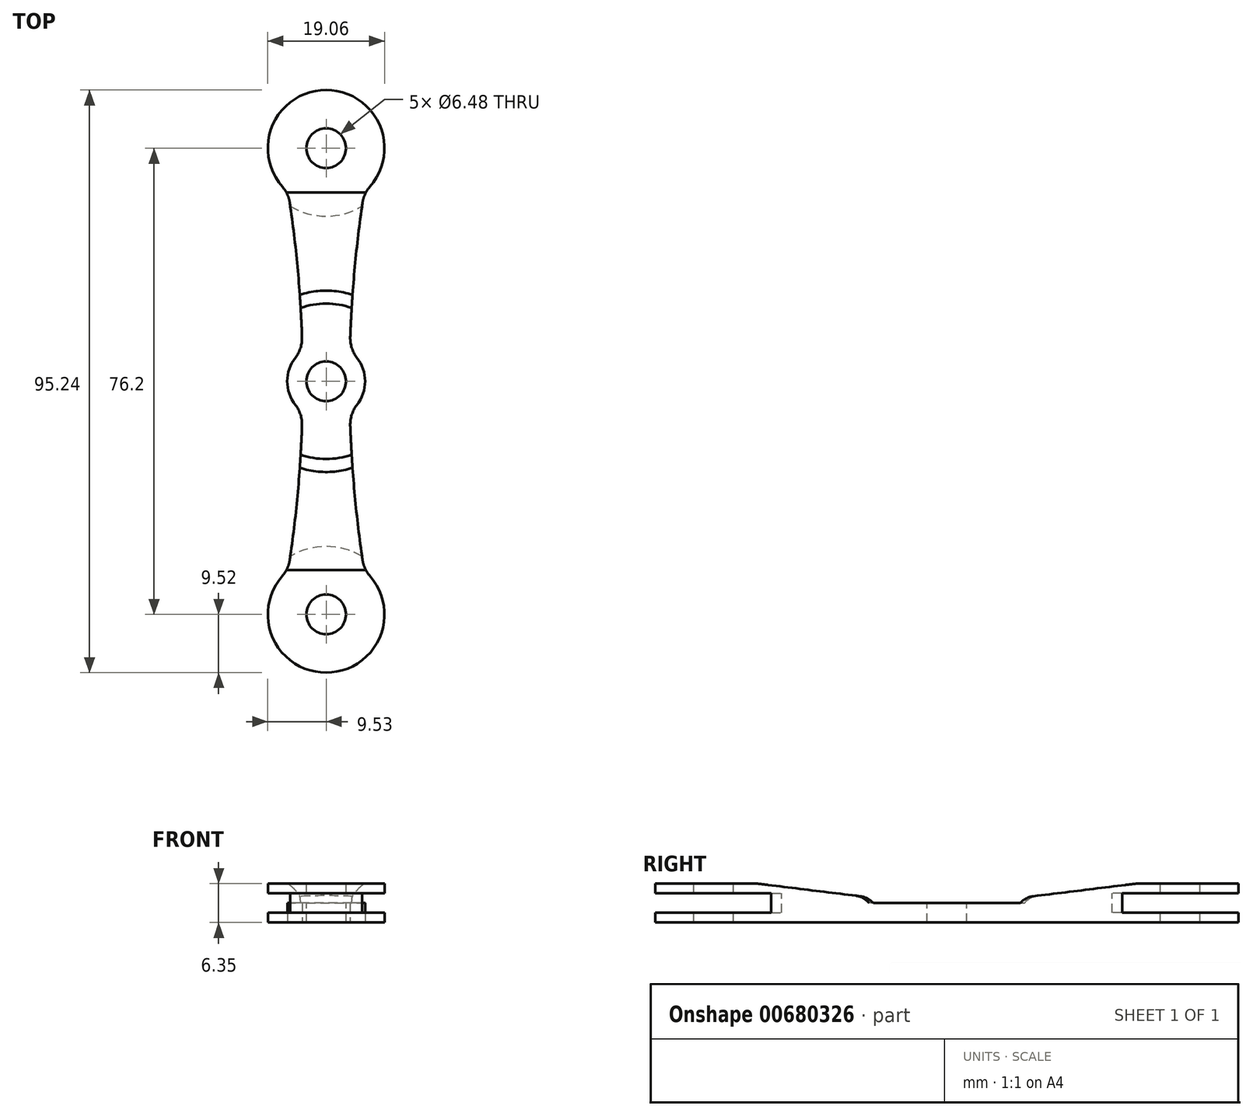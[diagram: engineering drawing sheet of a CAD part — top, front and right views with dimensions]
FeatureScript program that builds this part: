
annotation { "Feature Type Name" : "Feature", "Feature Type Description" : "" }
export const myFeature = defineFeature(function(context is Context, id is Id, definition is map)
    precondition{}
    {
        {
            var Q0;
            Q0=qCreatedBy(makeId("Top.planeOp"),FACE);
            var sketch = newSketch(context, id + "F0", { "sketchPlane" : qUnion([Q0])});
            skLineSegment(sketch, "E0.bottom", {"start": v(9.52, 47.63) * mm, "end": v(-9.53, 47.63) * mm});
            skLineSegment(sketch, "E0.top", {"start": v(9.52, -47.63) * mm, "end": v(-9.53, -47.63) * mm});
            skLineSegment(sketch, "E0.left", {"start": v(9.52, 47.63) * mm, "end": v(9.52, -47.63) * mm});
            skLineSegment(sketch, "E0.right", {"start": v(-9.52, 47.63) * mm, "end": v(-9.53, -47.63) * mm});
            skPoint(sketch, "E0.middle", {"position": v(0, 0) * mm});
            skCircle(sketch, "E1", {"center": v(0, 38.1) * mm, "radius": 9.53 * mm});
            skCircle(sketch, "E2", {"center": v(0, -38.1) * mm, "radius": 9.52 * mm});
            skCircle(sketch, "E3", {"center": v(0, 0) * mm, "radius": 6.35 * mm});
            skArc(sketch, "E4", {"start": v(-9.53, -47.62) * mm, "mid": v(-3.81, 0) * mm, "end": v(-9.53, 47.63) * mm});
            skArc(sketch, "E5", {"start": v(9.53, 47.62) * mm, "mid": v(3.81, 0) * mm, "end": v(9.53, -47.62) * mm});
            skSolve(sketch);
        }
        {
            var Q0;
            {var subQ0=sQuery(id+"F0.wireOp",EDGE,"E4");var subQ1=sQuery(id+"F0.wireOp",EDGE,"E3");var subQ2=makeQuery(id+"F0.imprint","INTERSECT",VERTEX,{"disambiguationData":[OD(0.0)],"derivedFrom":[subQ1,subQ0]});Q0=makeQuery(id+"F0.imprint","IMPRINT",FACE,{"disambiguationData":[TD([[makeQuery(id+"F0.imprint","IMPRINT",EDGE,{"disambiguationData":[TD([[subQ2,1.0]])],"derivedFrom":subQ1}),1.0]])]});}
            var Q1;
            {var subQ0=sQuery(id+"F0.wireOp",EDGE,"E5");var subQ1=sQuery(id+"F0.wireOp",EDGE,"E3");var subQ2=makeQuery(id+"F0.imprint","INTERSECT",VERTEX,{"disambiguationData":[OD(0.0)],"derivedFrom":[subQ1,subQ0]});Q1=makeQuery(id+"F0.imprint","IMPRINT",FACE,{"disambiguationData":[TD([[makeQuery(id+"F0.imprint","IMPRINT",EDGE,{"disambiguationData":[TD([[subQ2,1.0]])],"derivedFrom":subQ1}),1.0]])]});}
            var Q2;
            {var subQ0=sQuery(id+"F0.wireOp",EDGE,"E4");var subQ1=sQuery(id+"F0.wireOp",EDGE,"E3");var subQ2=makeQuery(id+"F0.imprint","INTERSECT",VERTEX,{"disambiguationData":[OD(0.0)],"derivedFrom":[subQ1,subQ0]});Q2=makeQuery(id+"F0.imprint","IMPRINT",FACE,{"disambiguationData":[TD([[makeQuery(id+"F0.imprint","IMPRINT",EDGE,{"disambiguationData":[TD([[subQ2,-1.0]])],"derivedFrom":subQ1}),1.0]])]});}
            var Q3;
            {var subQ0=sQuery(id+"F0.wireOp",EDGE,"E4");var subQ1=sQuery(id+"F0.wireOp",EDGE,"E1");var subQ2=makeQuery(id+"F0.imprint","INTERSECT",VERTEX,{"disambiguationData":[OD(1.0)],"derivedFrom":[subQ1,subQ0]});Q3=makeQuery(id+"F0.imprint","IMPRINT",FACE,{"disambiguationData":[TD([[makeQuery(id+"F0.imprint","IMPRINT",EDGE,{"disambiguationData":[TD([[subQ2,-1.0]])],"derivedFrom":subQ1}),-1.0]])]});}
            var Q4;
            {var subQ0=sQuery(id+"F0.wireOp",EDGE,"E5");var subQ1=sQuery(id+"F0.wireOp",EDGE,"E2");var subQ2=makeQuery(id+"F0.imprint","INTERSECT",VERTEX,{"disambiguationData":[OD(0.0)],"derivedFrom":[subQ1,subQ0]});Q4=makeQuery(id+"F0.imprint","IMPRINT",FACE,{"disambiguationData":[TD([[makeQuery(id+"F0.imprint","IMPRINT",EDGE,{"disambiguationData":[TD([[subQ2,-1.0]])],"derivedFrom":subQ1}),-1.0]])]});}
            var Q5;
            {var subQ0=sQuery(id+"F0.wireOp",EDGE,"E1");var subQ1=makeQuery(id+"F0.imprint","INTERSECT",VERTEX,{"derivedFrom":[sQuery(id+"F0.wireOp",EDGE,"E0.left"),subQ0]});Q5=makeQuery(id+"F0.imprint","IMPRINT",FACE,{"disambiguationData":[TD([[makeQuery(id+"F0.imprint","IMPRINT",EDGE,{"disambiguationData":[TD([[subQ1,-1.0]])],"derivedFrom":subQ0}),1.0]])]});}
            var Q6;
            {var subQ0=sQuery(id+"F0.wireOp",EDGE,"E1");var subQ1=makeQuery(id+"F0.imprint","INTERSECT",VERTEX,{"derivedFrom":[sQuery(id+"F0.wireOp",EDGE,"E0.right"),subQ0]});Q6=makeQuery(id+"F0.imprint","IMPRINT",FACE,{"disambiguationData":[TD([[makeQuery(id+"F0.imprint","IMPRINT",EDGE,{"disambiguationData":[TD([[subQ1,1.0]])],"derivedFrom":subQ0}),1.0]])]});}
            var Q7;
            {var subQ0=sQuery(id+"F0.wireOp",EDGE,"E2");var subQ1=makeQuery(id+"F0.imprint","INTERSECT",VERTEX,{"derivedFrom":[sQuery(id+"F0.wireOp",EDGE,"E0.left"),subQ0]});Q7=makeQuery(id+"F0.imprint","IMPRINT",FACE,{"disambiguationData":[TD([[makeQuery(id+"F0.imprint","IMPRINT",EDGE,{"disambiguationData":[TD([[subQ1,-1.0]])],"derivedFrom":subQ0}),1.0]])]});}
            var Q8;
            {var subQ0=sQuery(id+"F0.wireOp",EDGE,"E2");var subQ1=makeQuery(id+"F0.imprint","INTERSECT",VERTEX,{"derivedFrom":[sQuery(id+"F0.wireOp",EDGE,"E0.right"),subQ0]});Q8=makeQuery(id+"F0.imprint","IMPRINT",FACE,{"disambiguationData":[TD([[makeQuery(id+"F0.imprint","IMPRINT",EDGE,{"disambiguationData":[TD([[subQ1,1.0]])],"derivedFrom":subQ0}),1.0]])]});}
            var Q9;
            {var subQ1=sQuery(id+"F0.wireOp",EDGE,"E1");var subQ4=makeQuery(id+"F0.imprint","INTERSECT",VERTEX,{"derivedFrom":[sQuery(id+"F0.wireOp",EDGE,"E0.bottom"),subQ1]});Q9=makeQuery(id+"F0.imprint","IMPRINT",FACE,{"disambiguationData":[TD([[makeQuery(id+"F0.imprint","IMPRINT",EDGE,{"disambiguationData":[TD([[subQ4,1.0]])],"derivedFrom":subQ1}),1.0]])]});}
            var Q10;
            {var subQ1=sQuery(id+"F0.wireOp",EDGE,"E2");var subQ4=sQuery(id+"F0.wireOp",EDGE,"E5");var subQ5=makeQuery(id+"F0.imprint","INTERSECT",VERTEX,{"disambiguationData":[OD(0.0)],"derivedFrom":[subQ1,subQ4]});Q10=makeQuery(id+"F0.imprint","IMPRINT",FACE,{"disambiguationData":[TD([[makeQuery(id+"F0.imprint","IMPRINT",EDGE,{"disambiguationData":[TD([[subQ5,-1.0]])],"derivedFrom":subQ1}),1.0]])]});}
            extrude(context, id + "F1", {"entities" : qUnion([Q0, Q1, Q2, Q3, Q4, Q5, Q6, Q7, Q8, Q9, Q10]), "depth" : 6.35 * mm, "offsetDistance" : 25.4 * mm});
        }
        {
            var Q0;
            Q0=makeQuery(id+"F1.opExtrude","CAP_FACE",FACE,{"disambiguationData":[OSD([sQuery(id+"F0.wireOp",EDGE,"E1"),sQuery(id+"F0.wireOp",EDGE,"E2"),sQuery(id+"F0.wireOp",EDGE,"E3"),sQuery(id+"F0.wireOp",EDGE,"E4"),sQuery(id+"F0.wireOp",EDGE,"E5")])],"isStart":false});
            var sketch = newSketch(context, id + "F2", { "sketchPlane" : qUnion([Q0])});
            skCircle(sketch, "E6", {"center": v(0, 38.1) * mm, "radius": 3.24 * mm});
            skCircle(sketch, "E7", {"center": v(0, 0) * mm, "radius": 3.24 * mm});
            skCircle(sketch, "E8", {"center": v(0, -38.1) * mm, "radius": 3.24 * mm});
            skSolve(sketch);
        }
        {
            var Q0;
            Q0 = qSketchRegion(id + "F2", true);
            extrude(context, id + "F3", {"entities" : qUnion([Q0]), "operationType" : NewBodyOperationType.REMOVE, "endBound" : BoundingType.THROUGH_ALL, "oppositeDirection" : true, "depth" : 25.4 * mm, "offsetDistance" : 25.4 * mm});
        }
        {
            var Q0;
            Q0=qCreatedBy(makeId("Right.planeOp"),FACE);
            var sketch = newSketch(context, id + "F4", { "sketchPlane" : qUnion([Q0])});
            skPoint(sketch, "E9.0", {"position": v(-30.86, 6.35) * mm});
            skPoint(sketch, "E10.0", {"position": v(30.86, 6.35) * mm});
            skLineSegment(sketch, "E11", {"start": v(-30.86, 6.35) * mm, "end": v(30.86, 6.35) * mm});
            skPoint(sketch, "E12.0", {"position": v(-5.03, 3.18) * mm});
            skPoint(sketch, "E13.0", {"position": v(5.03, 3.18) * mm});
            skLineSegment(sketch, "E14", {"start": v(-30.86, 6.35) * mm, "end": v(-5.03, 3.18) * mm});
            skLineSegment(sketch, "E15", {"start": v(5.03, 3.18) * mm, "end": v(30.86, 6.35) * mm});
            skLineSegment(sketch, "E16", {"start": v(-5.03, 3.18) * mm, "end": v(5.03, 3.18) * mm});
            skSolve(sketch);
        }
        {
            var Q0;
            Q0 = qSketchRegion(id + "F4", true);
            extrude(context, id + "F5", {"entities" : qUnion([Q0]), "operationType" : NewBodyOperationType.REMOVE, "oppositeDirection" : true, "depth" : 25.4 * mm, "offsetDistance" : 25.4 * mm, "hasSecondDirection" : true, "secondDirectionOppositeDirection" : false, "secondDirectionDepth" : 25.4 * mm});
        }
        {
            var Q0;
            Q0=makeQuery(id+"F5.boolean.opBoolean","COPY",EDGE,{"derivedFrom":makeQuery(id+"F5.opExtrude","SWEPT_EDGE",EDGE,{"disambiguationData":[OSD([sQuery(id+"F4.wireOp",EDGE,"E11"),sQuery(id+"F4.wireOp",EDGE,"E14")])]})});
            var Q1;
            Q1=makeQuery(id+"F5.boolean.opBoolean","COPY",EDGE,{"derivedFrom":makeQuery(id+"F5.opExtrude","SWEPT_EDGE",EDGE,{"disambiguationData":[OSD([sQuery(id+"F4.wireOp",EDGE,"E11"),sQuery(id+"F4.wireOp",EDGE,"E15")])]})});
            var Q2;
            Q2=makeQuery(id+"F5.boolean.opBoolean","COPY",EDGE,{"derivedFrom":makeQuery(id+"F5.opExtrude","SWEPT_EDGE",EDGE,{"disambiguationData":[OSD([sQuery(id+"F4.wireOp",EDGE,"E14"),sQuery(id+"F4.wireOp",EDGE,"E16")])]})});
            var Q3;
            Q3=makeQuery(id+"F5.boolean.opBoolean","COPY",EDGE,{"derivedFrom":makeQuery(id+"F5.opExtrude","SWEPT_EDGE",EDGE,{"disambiguationData":[OSD([sQuery(id+"F4.wireOp",EDGE,"E15"),sQuery(id+"F4.wireOp",EDGE,"E16")])]})});
            var Q4;
            {var subQ0=sQuery(id+"F0.wireOp",EDGE,"E5");var subQ1=sQuery(id+"F0.wireOp",EDGE,"E3");Q4=makeQuery(id+"F1.opExtrude","SWEPT_EDGE",EDGE,{"disambiguationData":[OSD([subQ1,subQ0]),TDD([makeQuery(id+"F0.imprint","INTERSECT",VERTEX,{"disambiguationData":[OD(0.0)],"derivedFrom":[subQ1,subQ0]})])]});}
            var Q5;
            {var subQ0=sQuery(id+"F0.wireOp",EDGE,"E5");var subQ1=sQuery(id+"F0.wireOp",EDGE,"E3");Q5=makeQuery(id+"F1.opExtrude","SWEPT_EDGE",EDGE,{"disambiguationData":[OSD([subQ1,subQ0]),TDD([makeQuery(id+"F0.imprint","INTERSECT",VERTEX,{"disambiguationData":[OD(1.0)],"derivedFrom":[subQ1,subQ0]})])]});}
            var Q6;
            {var subQ0=sQuery(id+"F0.wireOp",EDGE,"E4");var subQ1=sQuery(id+"F0.wireOp",EDGE,"E3");Q6=makeQuery(id+"F1.opExtrude","SWEPT_EDGE",EDGE,{"disambiguationData":[OSD([subQ1,subQ0]),TDD([makeQuery(id+"F0.imprint","INTERSECT",VERTEX,{"disambiguationData":[OD(1.0)],"derivedFrom":[subQ1,subQ0]})])]});}
            var Q7;
            {var subQ0=sQuery(id+"F0.wireOp",EDGE,"E4");var subQ1=sQuery(id+"F0.wireOp",EDGE,"E3");Q7=makeQuery(id+"F1.opExtrude","SWEPT_EDGE",EDGE,{"disambiguationData":[OSD([subQ1,subQ0]),TDD([makeQuery(id+"F0.imprint","INTERSECT",VERTEX,{"disambiguationData":[OD(0.0)],"derivedFrom":[subQ1,subQ0]})])]});}
            var Q8;
            Q8=makeQuery(id+"F1.opExtrude","SWEPT_EDGE",EDGE,{"disambiguationData":[OSD([sQuery(id+"F0.wireOp",EDGE,"E2"),sQuery(id+"F0.wireOp",EDGE,"E4")])]});
            var Q9;
            Q9=makeQuery(id+"F1.opExtrude","SWEPT_EDGE",EDGE,{"disambiguationData":[OSD([sQuery(id+"F0.wireOp",EDGE,"E1"),sQuery(id+"F0.wireOp",EDGE,"E4")])]});
            var Q10;
            Q10=makeQuery(id+"F1.opExtrude","SWEPT_EDGE",EDGE,{"disambiguationData":[OSD([sQuery(id+"F0.wireOp",EDGE,"E1"),sQuery(id+"F0.wireOp",EDGE,"E5")])]});
            var Q11;
            Q11=makeQuery(id+"F1.opExtrude","SWEPT_EDGE",EDGE,{"disambiguationData":[OSD([sQuery(id+"F0.wireOp",EDGE,"E2"),sQuery(id+"F0.wireOp",EDGE,"E5")])]});
            fillet(context, id + "F6", {"entities" : qUnion([Q0, Q1, Q2, Q3, Q4, Q5, Q6, Q7, Q8, Q9, Q10, Q11]), "radius" : 5.08 * mm, "tangentPropagation" : true, "allowEdgeOverflow" : false});
        }
        {
            var Q0;
            {var subQ0=sQuery(id+"F0.wireOp",EDGE,"E5");var subQ1=sQuery(id+"F0.wireOp",EDGE,"E2");var subQ2=sQuery(id+"F0.wireOp",EDGE,"E3");var subQ3=sQuery(id+"F0.wireOp",EDGE,"E4");Q0=makeQuery(id+"F5.boolean.opBoolean","SPLIT",FACE,{"disambiguationData":[TD([makeQuery(id+"F1.opExtrude","SWEPT_FACE",FACE,{"disambiguationData":[OSD([subQ1])]})])],"derivedFrom":makeQuery(id+"F1.opExtrude","CAP_FACE",FACE,{"disambiguationData":[OSD([sQuery(id+"F0.wireOp",EDGE,"E1"),subQ1,subQ2,subQ3,subQ0])],"isStart":false})});}
            cPlane(context, id + "F7", {"entities" : qUnion([Q0]), "cplaneType" : CPlaneType.OFFSET, "offset" : 3.17 * mm, "oppositeDirection" : true, "width" : 152.4 * mm, "height" : 152.4 * mm});
        }
        {
            var Q0;
            Q0=qCreatedBy(id+"F7.planeOp",FACE);
            var sketch = newSketch(context, id + "F8", { "sketchPlane" : qUnion([Q0])});
            skCircle(sketch, "E17.0", {"center": v(0, -38.1) * mm, "radius": 3.24 * mm});
            skArc(sketch, "E18.0", {"start": v(-7.15, -31.8) * mm, "mid": v(0, -47.63) * mm, "end": v(7.15, -31.8) * mm});
            skCircle(sketch, "E19", {"center": v(0, -38.1) * mm, "radius": 9.52 * mm});
            skArc(sketch, "E20.0", {"start": v(7.15, 31.8) * mm, "mid": v(0, 47.63) * mm, "end": v(-7.15, 31.8) * mm});
            skCircle(sketch, "E21.0", {"center": v(0, 38.1) * mm, "radius": 3.24 * mm});
            skCircle(sketch, "E22", {"center": v(0, 38.1) * mm, "radius": 9.53 * mm});
            skSolve(sketch);
        }
        {
            var Q0;
            Q0 = qSketchRegion(id + "F8", true);
            extrude(context, id + "F9", {"entities" : qUnion([Q0]), "operationType" : NewBodyOperationType.REMOVE, "oppositeDirection" : true, "depth" : 1.59 * mm, "offsetDistance" : 25.4 * mm, "hasSecondDirection" : true, "secondDirectionOppositeDirection" : false, "secondDirectionDepth" : 1.59 * mm});
        }
        {
            var Q0;
            Q0=makeQuery(id+"F5.boolean.opBoolean","COPY",FACE,{"derivedFrom":makeQuery(id+"F5.opExtrude","SWEPT_FACE",FACE,{"disambiguationData":[OSD([sQuery(id+"F4.wireOp",EDGE,"E16")])]})});
            var sketch = newSketch(context, id + "F10", { "sketchPlane" : qUnion([Q0])});
            skCircle(sketch, "E23.0", {"center": v(0, 0) * mm, "radius": 3.24 * mm});
            skCircle(sketch, "E24", {"center": v(0, 0) * mm, "radius": 12.7 * mm});
            skSolve(sketch);
        }
        {
            var Q0;
            Q0 = qSketchRegion(id + "F10", true);
            extrude(context, id + "F11", {"entities" : qUnion([Q0]), "operationType" : NewBodyOperationType.REMOVE, "depth" : 25.4 * mm, "offsetDistance" : 25.4 * mm});
        }
        {
            var Q0;
            Q0=makeQuery(id+"F11.boolean.opBoolean","INTERSECT",EDGE,{"derivedFrom":[makeQuery(id+"F5.boolean.opBoolean","COPY",FACE,{"derivedFrom":makeQuery(id+"F5.opExtrude","SWEPT_FACE",FACE,{"disambiguationData":[OSD([sQuery(id+"F4.wireOp",EDGE,"E14")])]})}),makeQuery(id+"F11.opExtrude","SWEPT_FACE",FACE,{"disambiguationData":[OSD([sQuery(id+"F10.wireOp",EDGE,"E24")])]})]});
            var Q1;
            Q1=makeQuery(id+"F11.boolean.opBoolean","INTERSECT",EDGE,{"derivedFrom":[makeQuery(id+"F5.boolean.opBoolean","COPY",FACE,{"derivedFrom":makeQuery(id+"F5.opExtrude","SWEPT_FACE",FACE,{"disambiguationData":[OSD([sQuery(id+"F4.wireOp",EDGE,"E15")])]})}),makeQuery(id+"F11.opExtrude","SWEPT_FACE",FACE,{"disambiguationData":[OSD([sQuery(id+"F10.wireOp",EDGE,"E24")])]})]});
            fillet(context, id + "F12", {"entities" : qUnion([Q0, Q1]), "radius" : 3.17 * mm, "tangentPropagation" : true, "allowEdgeOverflow" : false});
        }
        {
            var Q0;
            Q0=qCreatedBy(id+"F7.planeOp",FACE);
            var sketch = newSketch(context, id + "F13", { "sketchPlane" : qUnion([Q0])});
            skCircle(sketch, "E25.0", {"center": v(0, -38.1) * mm, "radius": 9.52 * mm});
            skCircle(sketch, "E26.0", {"center": v(0, 38.1) * mm, "radius": 9.53 * mm});
            skCircle(sketch, "E27", {"center": v(0, 38.1) * mm, "radius": 11.11 * mm});
            skCircle(sketch, "E28", {"center": v(0, -38.1) * mm, "radius": 11.11 * mm});
            skSolve(sketch);
        }
        {
            var Q0;
            Q0 = qSketchRegion(id + "F13", true);
            extrude(context, id + "F14", {"entities" : qUnion([Q0]), "operationType" : NewBodyOperationType.REMOVE, "oppositeDirection" : true, "depth" : 1.59 * mm, "offsetDistance" : 25.4 * mm, "hasSecondDirection" : true, "secondDirectionOppositeDirection" : false, "secondDirectionDepth" : 1.59 * mm});
        }
    });
